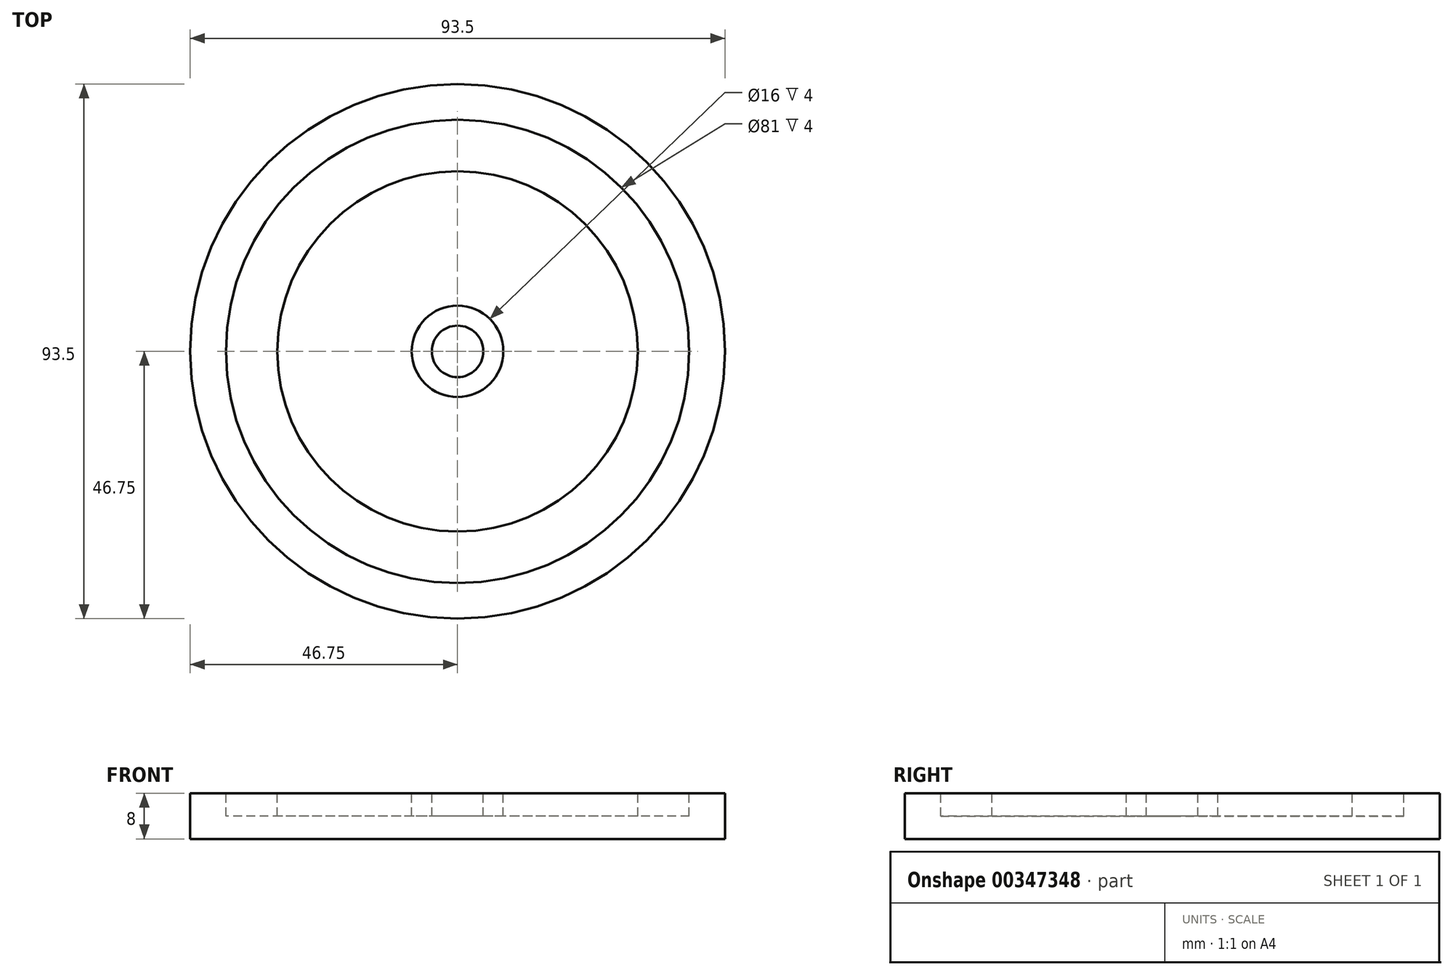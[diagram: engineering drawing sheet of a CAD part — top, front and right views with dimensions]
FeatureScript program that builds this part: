
annotation { "Feature Type Name" : "Feature", "Feature Type Description" : "" }
export const myFeature = defineFeature(function(context is Context, id is Id, definition is map)
    precondition{}
    {
        {
            var Q0;
            Q0=qCreatedBy(makeId("Top.planeOp"),FACE);
            var sketch = newSketch(context, id + "F0", { "sketchPlane" : qUnion([Q0])});
            skCircle(sketch, "E0", {"center": v(0, 0) * mm, "radius": 46.75 * mm});
            skSolve(sketch);
        }
        {
            var Q0;
            Q0=makeQuery(id+"F0.imprint","IMPRINT",FACE,{"disambiguationData":[TD([[makeQuery(id+"F0.imprint","IMPRINT",EDGE,{"derivedFrom":sQuery(id+"F0.wireOp",EDGE,"E0")}),1.0]])]});
            extrude(context, id + "F1", {"entities" : qUnion([Q0]), "depth" : 8 * mm});
        }
        {
            var Q0;
            Q0=makeQuery(id+"F1.opExtrude","CAP_FACE",FACE,{"disambiguationData":[OSD([sQuery(id+"F0.wireOp",EDGE,"E0")])],"isStart":false});
            var sketch = newSketch(context, id + "F2", { "sketchPlane" : qUnion([Q0])});
            skCircle(sketch, "E1", {"center": v(0, 0) * mm, "radius": 4.5 * mm});
            skCircle(sketch, "E2", {"center": v(0, 0) * mm, "radius": 8 * mm});
            skCircle(sketch, "E3", {"center": v(0, 0) * mm, "radius": 31.5 * mm});
            skCircle(sketch, "E4", {"center": v(0, 0) * mm, "radius": 40.5 * mm});
            skSolve(sketch);
        }
        {
            var Q0;
            Q0=makeQuery(id+"F2.imprint","IMPRINT",FACE,{"disambiguationData":[TD([[makeQuery(id+"F2.imprint","IMPRINT",EDGE,{"derivedFrom":sQuery(id+"F2.wireOp",EDGE,"E1")}),-1.0]])]});
            extrude(context, id + "F3", {"entities" : qUnion([Q0]), "operationType" : NewBodyOperationType.REMOVE, "oppositeDirection" : true, "depth" : 4 * mm});
        }
        {
            var Q0;
            Q0=makeQuery(id+"F2.imprint","IMPRINT",FACE,{"disambiguationData":[TD([[makeQuery(id+"F2.imprint","IMPRINT",EDGE,{"derivedFrom":sQuery(id+"F2.wireOp",EDGE,"E3")}),-1.0]])]});
            extrude(context, id + "F4", {"entities" : qUnion([Q0]), "operationType" : NewBodyOperationType.REMOVE, "oppositeDirection" : true, "depth" : 4 * mm});
        }
    });
